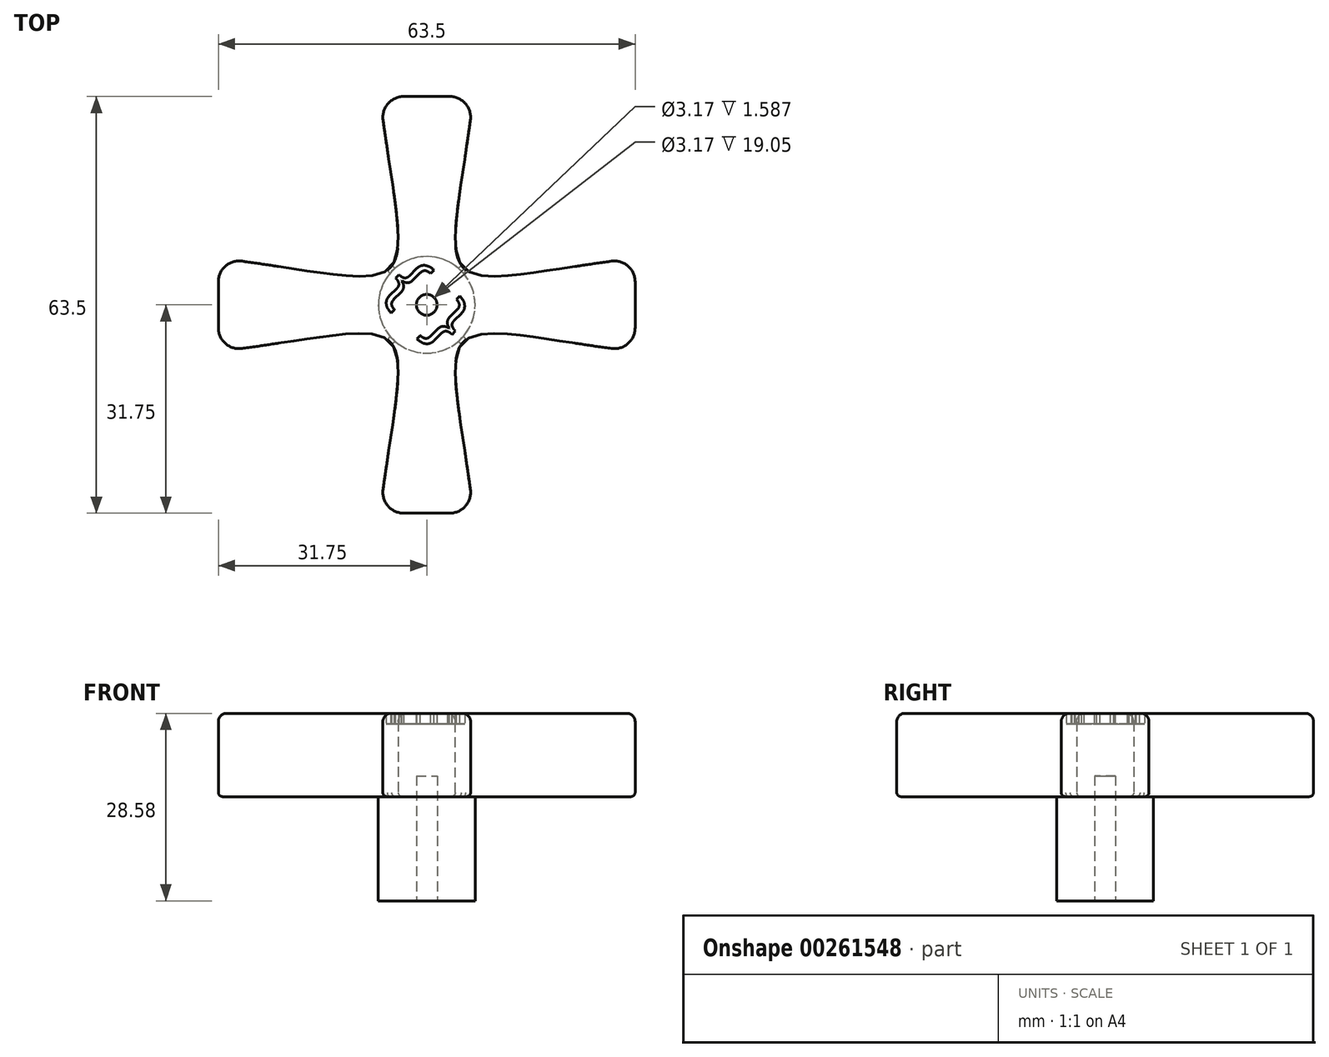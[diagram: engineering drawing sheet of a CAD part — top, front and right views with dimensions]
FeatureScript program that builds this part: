
annotation { "Feature Type Name" : "Feature", "Feature Type Description" : "" }
export const myFeature = defineFeature(function(context is Context, id is Id, definition is map)
    precondition{}
    {
        {
            var Q0;
            Q0=qCreatedBy(makeId("Top.planeOp"),FACE);
            var sketch = newSketch(context, id + "F0", { "sketchPlane" : qUnion([Q0])});
            skLineSegment(sketch, "E0", {"start": v(0, 0) * mm, "end": v(0, 31.75) * mm, "construction": true});
            skLineSegment(sketch, "E1", {"start": v(-31.75, 0) * mm, "end": v(0, 0) * mm, "construction": true});
            skLineSegment(sketch, "E2", {"start": v(31.75, 0) * mm, "end": v(0, 0) * mm, "construction": true});
            skLineSegment(sketch, "E3", {"start": v(0, -31.75) * mm, "end": v(0, 0) * mm, "construction": true});
            skLineSegment(sketch, "E4", {"start": v(-31.75, 7.14) * mm, "end": v(-31.75, -7.14) * mm});
            skLineSegment(sketch, "E5", {"start": v(-7.14, -31.75) * mm, "end": v(7.14, -31.75) * mm});
            skLineSegment(sketch, "E6", {"start": v(31.75, -7.14) * mm, "end": v(31.75, 7.14) * mm});
            skLineSegment(sketch, "E7", {"start": v(-7.14, 31.75) * mm, "end": v(7.14, 31.75) * mm});
            skCircle(sketch, "E8", {"center": v(0, 0) * mm, "radius": 15.88 * mm, "construction": true});
            skLineSegment(sketch, "E9", {"start": v(-15.88, 5.08) * mm, "end": v(-15.88, -5.08) * mm, "construction": true});
            skCircle(sketch, "E10", {"center": v(0, 0) * mm, "radius": 7.94 * mm, "construction": true});
            skLineSegment(sketch, "E11", {"start": v(-5.08, -15.88) * mm, "end": v(5.08, -15.88) * mm, "construction": true});
            skLineSegment(sketch, "E12.MirrorCS", {"start": v(0, 0) * mm, "end": v(0, -31.75) * mm, "construction": true});
            skLineSegment(sketch, "E13", {"start": v(-5.61, -5.61) * mm, "end": v(5.61, 5.61) * mm, "construction": true});
            skFitSpline(sketch, "E14", {"points": [v(-31.75, -7.14) * mm, v(-5.61, -5.61) * mm, v(-7.14, -31.75) * mm], "startDerivative": vector(95.25, 12.38) * mm, "endDerivative": vector(-12.38, -95.25) * mm});
            skFitSpline(sketch, "E15.MirrorCS", {"points": [v(31.75, -7.14) * mm, v(5.61, -5.61) * mm, v(7.14, -31.75) * mm], "startDerivative": vector(-95.25, 12.38) * mm, "endDerivative": vector(12.38, -95.25) * mm});
            skFitSpline(sketch, "E16.MirrorCS", {"points": [v(-31.75, 7.14) * mm, v(-5.61, 5.61) * mm, v(-7.14, 31.75) * mm], "startDerivative": vector(95.25, -12.38) * mm, "endDerivative": vector(-12.38, 95.25) * mm});
            skFitSpline(sketch, "E17.MirrorCS", {"points": [v(31.75, 7.14) * mm, v(5.61, 5.61) * mm, v(7.14, 31.75) * mm], "startDerivative": vector(-95.25, -12.38) * mm, "endDerivative": vector(12.38, 95.25) * mm});
            skSolve(sketch);
        }
        {
            var Q0;
            Q0=qSketchRegion(id+"F0",true);
            extrude(context, id + "F1", {"entities" : qUnion([Q0]), "depth" : 12.7 * mm});
        }
        {
            var Q0;
            Q0=makeQuery(id+"F1.opExtrude","CAP_FACE",FACE,{"disambiguationData":[OSD([sQuery(id+"F0.wireOp",EDGE,"E4"),sQuery(id+"F0.wireOp",EDGE,"E5"),sQuery(id+"F0.wireOp",EDGE,"E6"),sQuery(id+"F0.wireOp",EDGE,"E7"),sQuery(id+"F0.wireOp",EDGE,"E14"),sQuery(id+"F0.wireOp",EDGE,"E15.MirrorCS"),sQuery(id+"F0.wireOp",EDGE,"E16.MirrorCS"),sQuery(id+"F0.wireOp",EDGE,"E17.MirrorCS")])],"isStart":true});
            var sketch = newSketch(context, id + "F2", { "sketchPlane" : qUnion([Q0])});
            skCircle(sketch, "E18", {"center": v(0, 0) * mm, "radius": 7.37 * mm});
            skSolve(sketch);
        }
        {
            var Q0;
            Q0=qSketchRegion(id+"F2",true);
            extrude(context, id + "F3", {"entities" : qUnion([Q0]), "operationType" : NewBodyOperationType.ADD, "depth" : 15.88 * mm});
        }
        {
            var Q0;
            Q0=makeQuery(id+"FHBKJaG82kfliYF_1.boolean.opBoolean","MERGE",FACE,{"derivedFrom":[makeQuery(id+"F1.opExtrude","CAP_FACE",FACE,{"disambiguationData":[OSD([sQuery(id+"F0.wireOp",EDGE,"E4"),sQuery(id+"F0.wireOp",EDGE,"E5"),sQuery(id+"F0.wireOp",EDGE,"E6"),sQuery(id+"F0.wireOp",EDGE,"E7"),sQuery(id+"F0.wireOp",EDGE,"E14"),sQuery(id+"F0.wireOp",EDGE,"E15.MirrorCS"),sQuery(id+"F0.wireOp",EDGE,"E16.MirrorCS"),sQuery(id+"F0.wireOp",EDGE,"E17.MirrorCS")])],"isStart":false}),makeQuery(id+"FHBKJaG82kfliYF_1.opExtrude","CAP_FACE",FACE,{"disambiguationData":[OSD([sQuery(id+"FlcRGu9XOME26Uw_1.wireOp",EDGE,"4aeb7ee9-712b-4c87-8b6b-3736a43f95a2"),sQuery(id+"FlcRGu9XOME26Uw_1.wireOp",EDGE,"5124bdd7-5500-46ca-ada0-c6f18179f70a0.MirrorCS"),sQuery(id+"FlcRGu9XOME26Uw_1.wireOp",EDGE,"3c1a6850-1179-4b00-b570-ccdac5f7884b0.MirrorCS"),sQuery(id+"FlcRGu9XOME26Uw_1.wireOp",EDGE,"ff6566bc-f724-427d-8e95-42f8fa4ef3770.MirrorCS"),sQuery(id+"FlcRGu9XOME26Uw_1.wireOp",EDGE,"qXK4DlwG-7KnT-G8Oz-TqMb-Z13vw5oB3guk"),sQuery(id+"FlcRGu9XOME26Uw_1.wireOp",EDGE,"dqaNWhFM-M3ve-srLk-W5Z1-zQcwXBHqWryK"),sQuery(id+"FlcRGu9XOME26Uw_1.wireOp",EDGE,"r9uwT2Yu-TUu2-pDg3-xqRF-IJZkSwj9vNKo"),sQuery(id+"FlcRGu9XOME26Uw_1.wireOp",EDGE,"dcotBPHB-oE0p-CpJw-bHCk-VDZde19CIVf2")])],"isStart":true})]});
            var sketch = newSketch(context, id + "F4", { "sketchPlane" : qUnion([Q0])});
            skText(sketch, "E19", { "text": "{", "fontName": "OpenSans-Regular.ttf"});
            skText(sketch, "E20", { "text": "}", "fontName": "OpenSans-Regular.ttf"});
            skLineSegment(sketch, "E21", {"start": v(-3.74, -0.57) * mm, "end": v(-0.57, -3.74) * mm, "construction": true});
            skLineSegment(sketch, "E22", {"start": v(-2.16, -2.16) * mm, "end": v(9.66, 9.66) * mm, "construction": true});
            skLineSegment(sketch, "E23", {"start": v(-2.81, 2.74) * mm, "end": v(3.1, -3.17) * mm, "construction": true});
            skCircle(sketch, "E24", {"center": v(0, 0) * mm, "radius": 1.59 * mm});
            skLineSegment(sketch, "E25", {"start": v(0, 0) * mm, "end": v(31.75, 0) * mm, "construction": true});
            skLineSegment(sketch, "E26", {"start": v(0, 0) * mm, "end": v(0, -31.75) * mm, "construction": true});
            const initialGuessF4  = {"E19": [-0.0068, 0.0025, 0.7071, -0.7071, 0.00762], "E20": [-0.00057, -0.00374, 0.7071, -0.7071, 0.00762]};
            skSetInitialGuess(sketch, initialGuessF4);
            skSolve(sketch);
        }
        {
            var Q0;
            Q0=qSketchRegion(id+"F4",true);
            extrude(context, id + "F5", {"entities" : qUnion([Q0]), "operationType" : NewBodyOperationType.REMOVE, "oppositeDirection" : true, "depth" : 1.59 * mm});
        }
        {
            var Q0;
            Q0=makeQuery(id+"F1.opExtrude","SWEPT_EDGE",EDGE,{"disambiguationData":[OSD([sQuery(id+"F0.wireOp",EDGE,"E5"),sQuery(id+"F0.wireOp",EDGE,"E15.MirrorCS")])]});
            var Q1;
            Q1=makeQuery(id+"F1.opExtrude","SWEPT_EDGE",EDGE,{"disambiguationData":[OSD([sQuery(id+"F0.wireOp",EDGE,"E6"),sQuery(id+"F0.wireOp",EDGE,"E15.MirrorCS")])]});
            var Q2;
            Q2=makeQuery(id+"F1.opExtrude","SWEPT_EDGE",EDGE,{"disambiguationData":[OSD([sQuery(id+"F0.wireOp",EDGE,"E6"),sQuery(id+"F0.wireOp",EDGE,"E17.MirrorCS")])]});
            var Q3;
            Q3=makeQuery(id+"F1.opExtrude","SWEPT_EDGE",EDGE,{"disambiguationData":[OSD([sQuery(id+"F0.wireOp",EDGE,"E7"),sQuery(id+"F0.wireOp",EDGE,"E17.MirrorCS")])]});
            var Q4;
            Q4=makeQuery(id+"F1.opExtrude","SWEPT_EDGE",EDGE,{"disambiguationData":[OSD([sQuery(id+"F0.wireOp",EDGE,"E7"),sQuery(id+"F0.wireOp",EDGE,"E16.MirrorCS")])]});
            var Q5;
            Q5=makeQuery(id+"F1.opExtrude","SWEPT_EDGE",EDGE,{"disambiguationData":[OSD([sQuery(id+"F0.wireOp",EDGE,"E4"),sQuery(id+"F0.wireOp",EDGE,"E14")])]});
            var Q6;
            Q6=makeQuery(id+"F1.opExtrude","SWEPT_EDGE",EDGE,{"disambiguationData":[OSD([sQuery(id+"F0.wireOp",EDGE,"E4"),sQuery(id+"F0.wireOp",EDGE,"E16.MirrorCS")])]});
            var Q7;
            Q7=makeQuery(id+"F1.opExtrude","SWEPT_EDGE",EDGE,{"disambiguationData":[OSD([sQuery(id+"F0.wireOp",EDGE,"E5"),sQuery(id+"F0.wireOp",EDGE,"E14")])]});
            fillet(context, id + "F6", {"entities" : qUnion([Q0, Q1, Q2, Q3, Q4, Q5, Q6, Q7]), "radius" : 3.17 * mm, "tangentPropagation" : true, "allowEdgeOverflow" : false});
        }
        {
            var Q0;
            Q0=makeQuery(id+"F1.opExtrude","CAP_EDGE",EDGE,{"disambiguationData":[OSD([sQuery(id+"F0.wireOp",EDGE,"E14")])],"isStart":false});
            fillet(context, id + "F7", {"entities" : qUnion([Q0]), "radius" : 1.27 * mm, "tangentPropagation" : true, "allowEdgeOverflow" : false});
        }
        {
            var Q0;
            Q0=makeQuery(id+"F1.opExtrude","CAP_EDGE",EDGE,{"disambiguationData":[OSD([sQuery(id+"F0.wireOp",EDGE,"E16.MirrorCS")])],"isStart":true});
            fillet(context, id + "F8", {"entities" : qUnion([Q0]), "radius" : 0.64 * mm, "tangentPropagation" : true, "allowEdgeOverflow" : false});
        }
        {
            var Q0;
            Q0=makeQuery(id+"F3.opExtrude","CAP_FACE",FACE,{"disambiguationData":[OSD([sQuery(id+"F2.wireOp",EDGE,"E18")])],"isStart":false});
            var sketch = newSketch(context, id + "F9", { "sketchPlane" : qUnion([Q0])});
            skCircle(sketch, "E27", {"center": v(0, 0) * mm, "radius": 1.59 * mm});
            skSolve(sketch);
        }
        {
            var Q0;
            Q0 = qSketchRegion(id + "F9", true);
            extrude(context, id + "F10", {"entities" : qUnion([Q0]), "operationType" : NewBodyOperationType.REMOVE, "oppositeDirection" : true, "depth" : 19.05 * mm, "offsetDistance" : 25.4 * mm});
        }
    });
